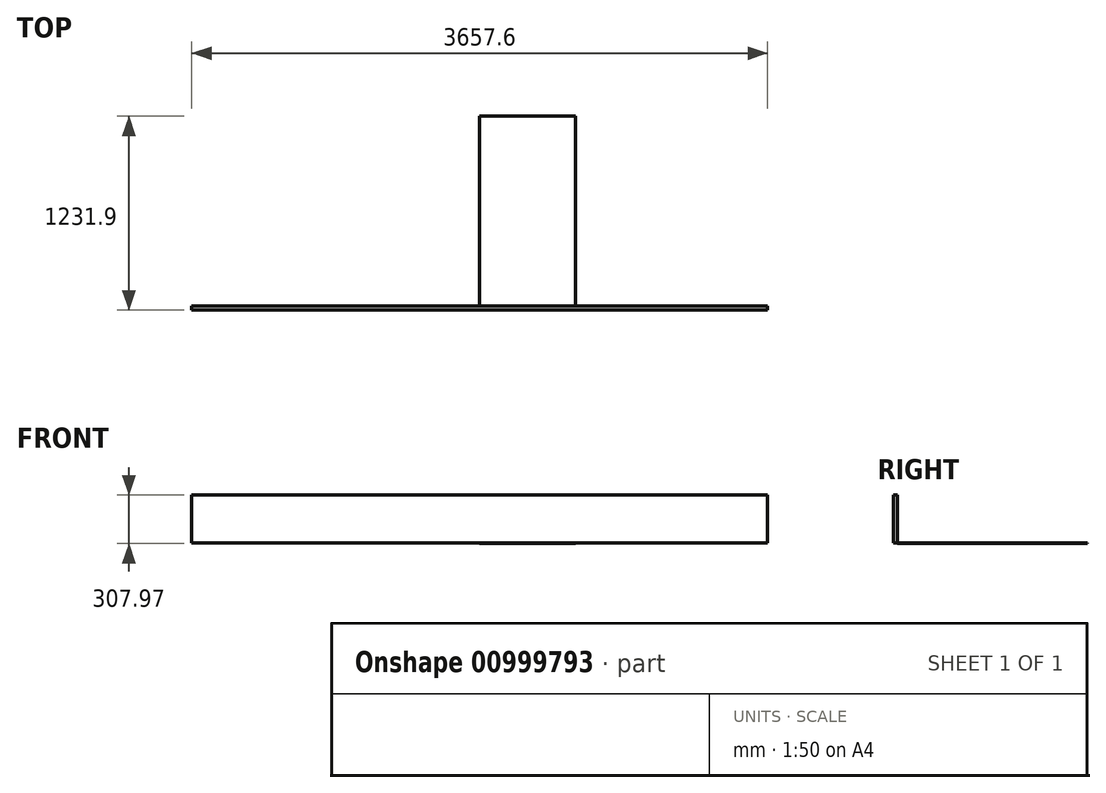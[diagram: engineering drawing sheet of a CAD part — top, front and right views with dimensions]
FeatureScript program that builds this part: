
annotation { "Feature Type Name" : "Feature", "Feature Type Description" : "" }
export const myFeature = defineFeature(function(context is Context, id is Id, definition is map)
    precondition{}
    {
        {
            var Q0;
            Q0=qCreatedBy(makeId("Right.planeOp"),FACE);
            var sketch = newSketch(context, id + "F0", { "sketchPlane" : qUnion([Q0])});
            skLineSegment(sketch, "E0.bottom", {"start": v(12.7, 152.4) * mm, "end": v(-12.7, 152.4) * mm});
            skLineSegment(sketch, "E0.top", {"start": v(12.7, -152.4) * mm, "end": v(-12.7, -152.4) * mm});
            skLineSegment(sketch, "E0.left", {"start": v(12.7, 152.4) * mm, "end": v(12.7, -152.4) * mm});
            skLineSegment(sketch, "E0.right", {"start": v(-12.7, 152.4) * mm, "end": v(-12.7, -152.4) * mm});
            skPoint(sketch, "E0.middle", {"position": v(0, 0) * mm});
            skSolve(sketch);
        }
        {
            var Q0;
            Q0=makeQuery(id+"F0.imprint","IMPRINT",FACE,{"disambiguationData":[TD([[makeQuery(id+"F0.imprint","IMPRINT",EDGE,{"derivedFrom":sQuery(id+"F0.wireOp",EDGE,"E0.bottom")}),1.0]])]});
            extrude(context, id + "F1", {"entities" : qUnion([Q0]), "depth" : 3657.6 * mm, "offsetDistance" : 25.4 * mm, "symmetric" : true});
        }
        {
            var Q0;
            Q0=makeQuery(id+"F1.opExtrude","SWEPT_FACE",FACE,{"disambiguationData":[OSD([sQuery(id+"F0.wireOp",EDGE,"E0.top")])]});
            var sketch = newSketch(context, id + "F2", { "sketchPlane" : qUnion([Q0])});
            skLineSegment(sketch, "E1.bottom", {"start": v(0, 0) * mm, "end": v(609.6, 0) * mm});
            skLineSegment(sketch, "E1.top", {"start": v(0, -1219.2) * mm, "end": v(609.6, -1219.2) * mm});
            skLineSegment(sketch, "E1.left", {"start": v(0, 0) * mm, "end": v(0, -1219.2) * mm});
            skLineSegment(sketch, "E1.right", {"start": v(609.6, 0) * mm, "end": v(609.6, -1219.2) * mm});
            skSolve(sketch);
        }
        {
            var Q0;
            {var subQ0=sQuery(id+"F2.wireOp",EDGE,"E1.top");Q0=makeQuery(id+"F2.imprint","IMPRINT",FACE,{"disambiguationData":[TD([[makeQuery(id+"F2.imprint","IMPRINT",EDGE,{"derivedFrom":subQ0}),1.0]])]});}
            extrude(context, id + "F3", {"entities" : qUnion([Q0]), "depth" : 3.17 * mm, "offsetDistance" : 25.4 * mm});
        }
    });
